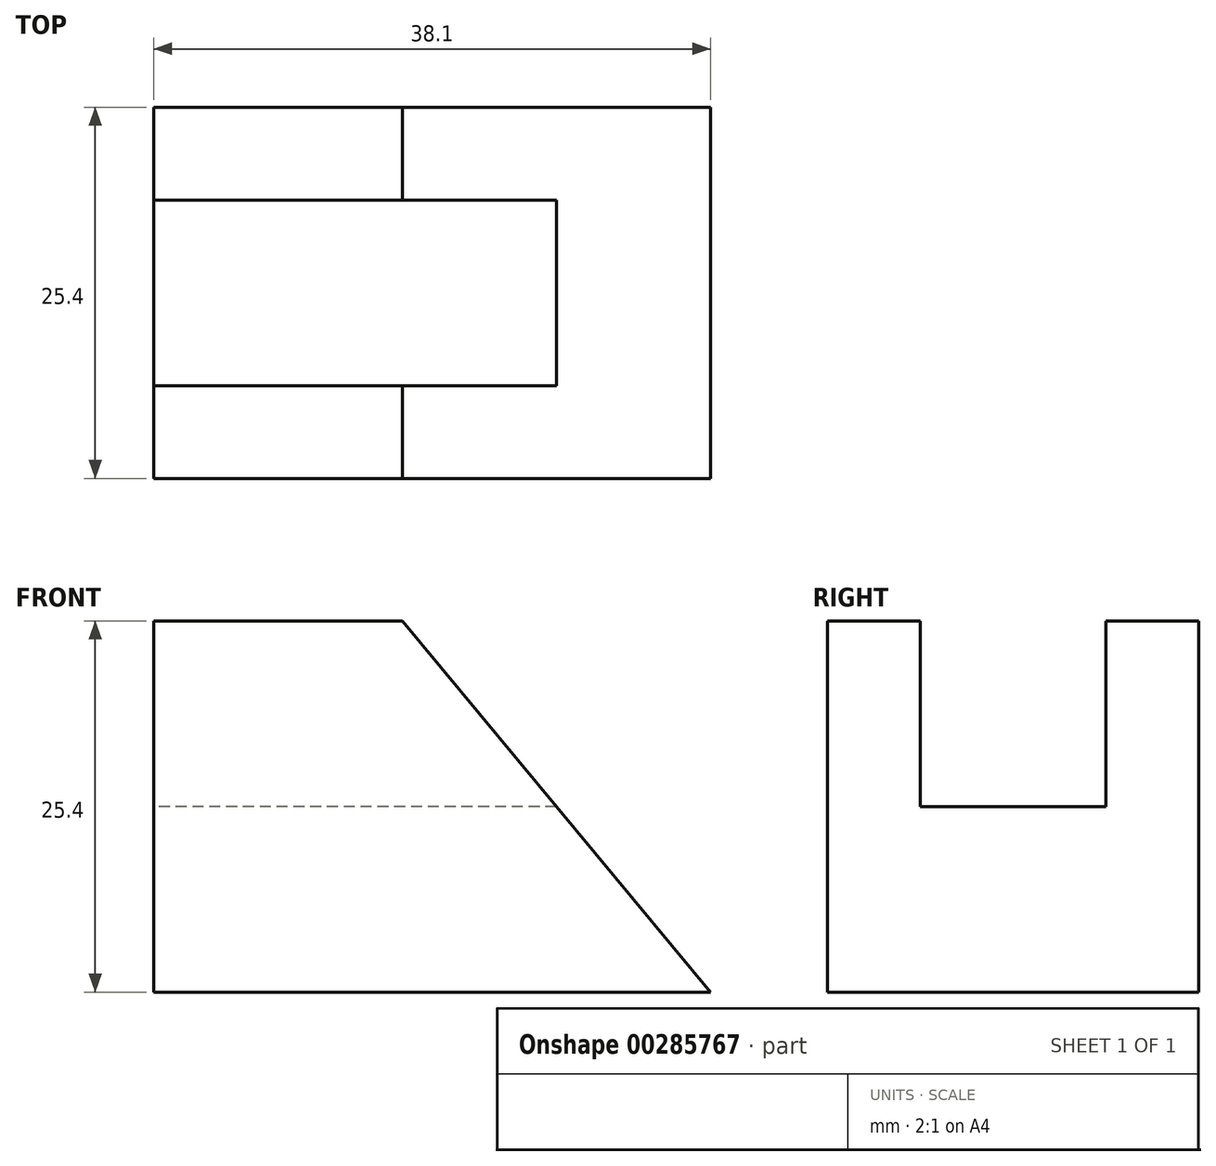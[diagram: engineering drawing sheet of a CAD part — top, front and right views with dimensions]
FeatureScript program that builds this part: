
annotation { "Feature Type Name" : "Feature", "Feature Type Description" : "" }
export const myFeature = defineFeature(function(context is Context, id is Id, definition is map)
    precondition{}
    {
        {
            var Q0;
            Q0=qCreatedBy(makeId("Front.planeOp"),FACE);
            var sketch = newSketch(context, id + "F0", { "sketchPlane" : qUnion([Q0])});
            skLineSegment(sketch, "E0.bottom", {"start": v(0, 0) * mm, "end": v(38.1, 0) * mm});
            skLineSegment(sketch, "E0.top", {"start": v(0, 25.4) * mm, "end": v(38.1, 25.4) * mm});
            skLineSegment(sketch, "E0.left", {"start": v(0, 0) * mm, "end": v(0, 25.4) * mm});
            skLineSegment(sketch, "E0.right", {"start": v(38.1, 0) * mm, "end": v(38.1, 25.4) * mm});
            skSolve(sketch);
        }
        {
            var Q0;
            Q0 = qSketchRegion(id + "F0", true);
            extrude(context, id + "F1", {"entities" : qUnion([Q0]), "endBound" : BoundingType.SYMMETRIC, "depth" : 25.4 * mm});
        }
        {
            var Q0;
            Q0=qCreatedBy(makeId("Front.planeOp"),FACE);
            var sketch = newSketch(context, id + "F2", { "sketchPlane" : qUnion([Q0])});
            skLineSegment(sketch, "E1", {"start": v(17.01, 25.4) * mm, "end": v(38.1, 0) * mm});
            skLineSegment(sketch, "E2", {"start": v(17.01, 25.4) * mm, "end": v(38.1, 25.4) * mm});
            skLineSegment(sketch, "E3", {"start": v(38.1, 25.4) * mm, "end": v(38.1, 0) * mm});
            skSolve(sketch);
        }
        {
            var Q0;
            Q0 = qSketchRegion(id + "F2", true);
            extrude(context, id + "F3", {"entities" : qUnion([Q0]), "operationType" : NewBodyOperationType.REMOVE, "endBound" : BoundingType.SYMMETRIC, "oppositeDirection" : true, "depth" : 25.4 * mm});
        }
        {
            var Q0;
            Q0=qCreatedBy(makeId("Right.planeOp"),FACE);
            var sketch = newSketch(context, id + "F4", { "sketchPlane" : qUnion([Q0])});
            skLineSegment(sketch, "E4.bottom", {"start": v(-6.35, 25.4) * mm, "end": v(6.35, 25.4) * mm});
            skLineSegment(sketch, "E4.top", {"start": v(-6.35, 12.7) * mm, "end": v(6.35, 12.7) * mm});
            skLineSegment(sketch, "E4.left", {"start": v(-6.35, 25.4) * mm, "end": v(-6.35, 12.7) * mm});
            skLineSegment(sketch, "E4.right", {"start": v(6.35, 25.4) * mm, "end": v(6.35, 12.7) * mm});
            skSolve(sketch);
        }
        {
            var Q0;
            Q0 = qSketchRegion(id + "F4", true);
            extrude(context, id + "F5", {"entities" : qUnion([Q0]), "operationType" : NewBodyOperationType.REMOVE, "depth" : 50.8 * mm});
        }
    });
